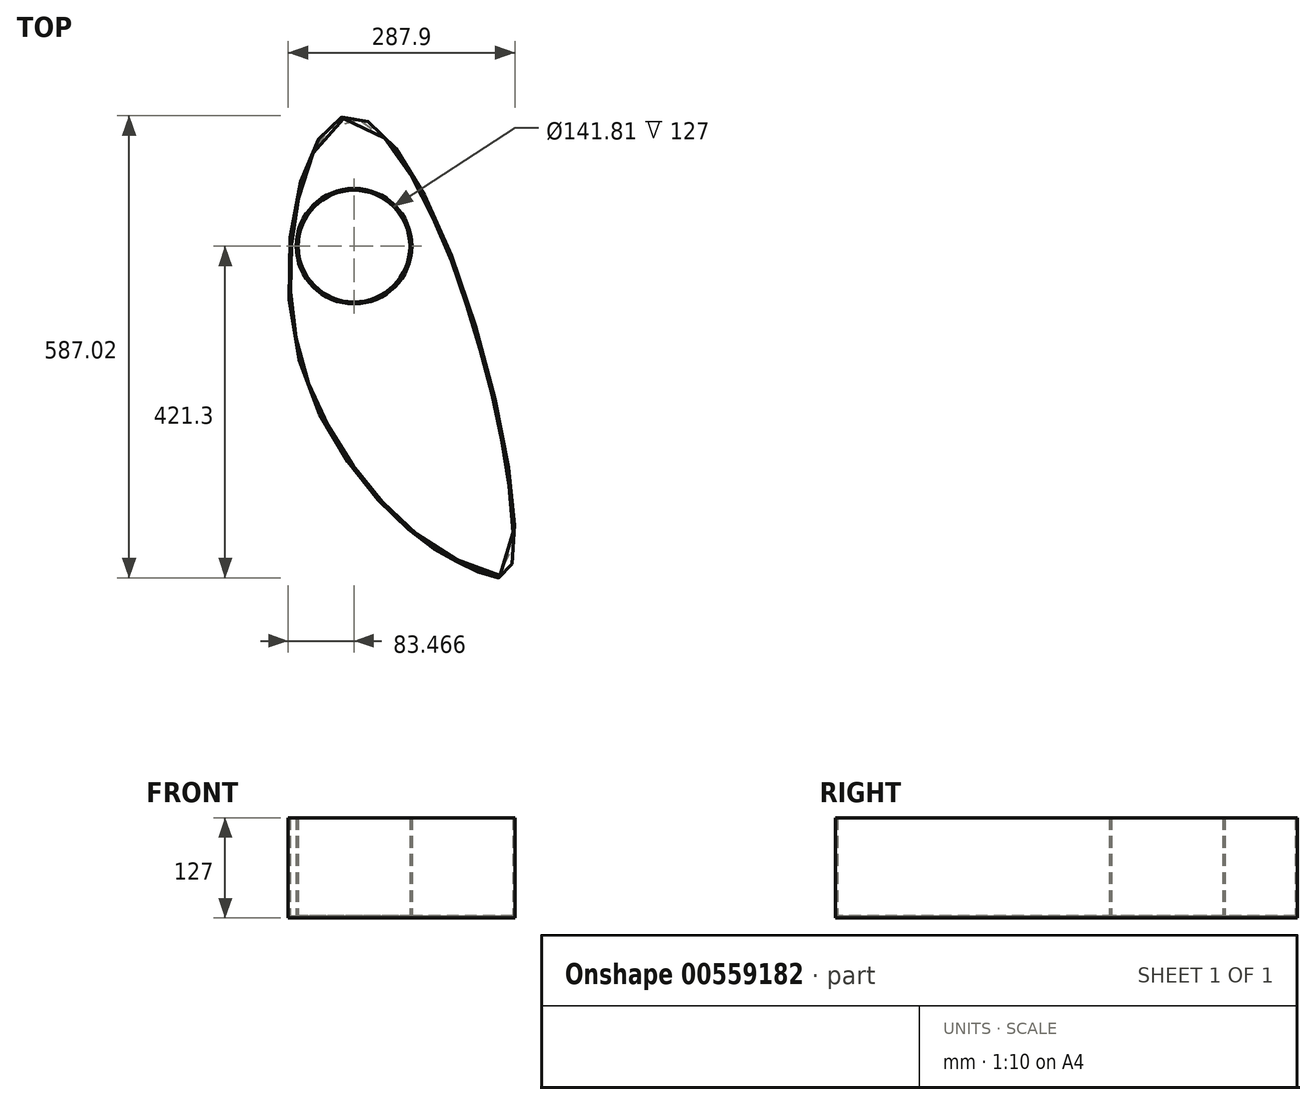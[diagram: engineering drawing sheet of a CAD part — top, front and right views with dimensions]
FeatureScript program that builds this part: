
annotation { "Feature Type Name" : "Feature", "Feature Type Description" : "" }
export const myFeature = defineFeature(function(context is Context, id is Id, definition is map)
    precondition{}
    {
        {
            var Q0;
            Q0=qCreatedBy(makeId("Top.planeOp"),FACE);
            var sketch = newSketch(context, id + "F0", { "sketchPlane" : qUnion([Q0])});
            skFitSpline(sketch, "E0", {"points": [v(579.05, -12.2) * mm, v(649.72, -416.17) * mm, v(605.55, -410.27) * mm, v(533.4, -367.52) * mm, v(378.82, -115.4) * mm, v(437.7, 163.24) * mm, v(579.05, -12.2) * mm]});
            skCircle(sketch, "E1", {"center": v(455.38, 0) * mm, "radius": 70.9 * mm});
            skCircle(sketch, "E2", {"center": v(455.38, 0) * mm, "radius": 28.43 * mm});
            skSolve(sketch);
        }
        {
            var Q0;
            Q0 = qSketchRegion(id + "F0", true);
            extrude(context, id + "F1", {"entities" : qUnion([Q0]), "depth" : 127 * mm, "offsetDistance" : 25.4 * mm});
        }
        {
            var Q0;
            Q0=makeQuery(id+"F1.opExtrude","CAP_FACE",FACE,{"disambiguationData":[OSD([sQuery(id+"F0.wireOp",EDGE,"E0"),sQuery(id+"F0.wireOp",EDGE,"E1")])],"isStart":false});
            shell(context, id + "F2", {"entities" : qUnion([Q0]), "thickness" : 2.54 * mm});
        }
        {
            var Q0;
            Q0=qCreatedBy(makeId("Top.planeOp"),FACE);
            var sketch = newSketch(context, id + "F3", { "sketchPlane" : qUnion([Q0])});
            skPoint(sketch, "E3", {"position": v(1640.4, -1276.64) * mm});
            skPoint(sketch, "E4", {"position": v(1362.9, -1310.75) * mm});
            skPoint(sketch, "E5", {"position": v(1062.01, -924.6) * mm});
            skPoint(sketch, "E6", {"position": v(784.22, -1135.42) * mm});
            skCircle(sketch, "E7", {"center": v(2776, 1919.7) * mm, "radius": 2343.44 * mm});
            skCircle(sketch, "E8", {"center": v(2776, 1919.7) * mm, "radius": 553.52 * mm});
            skLineSegment(sketch, "E9", {"start": v(1326.12, -661.15) * mm, "end": v(170.65, 2059.33) * mm});
            skSolve(sketch);
        }
    });
